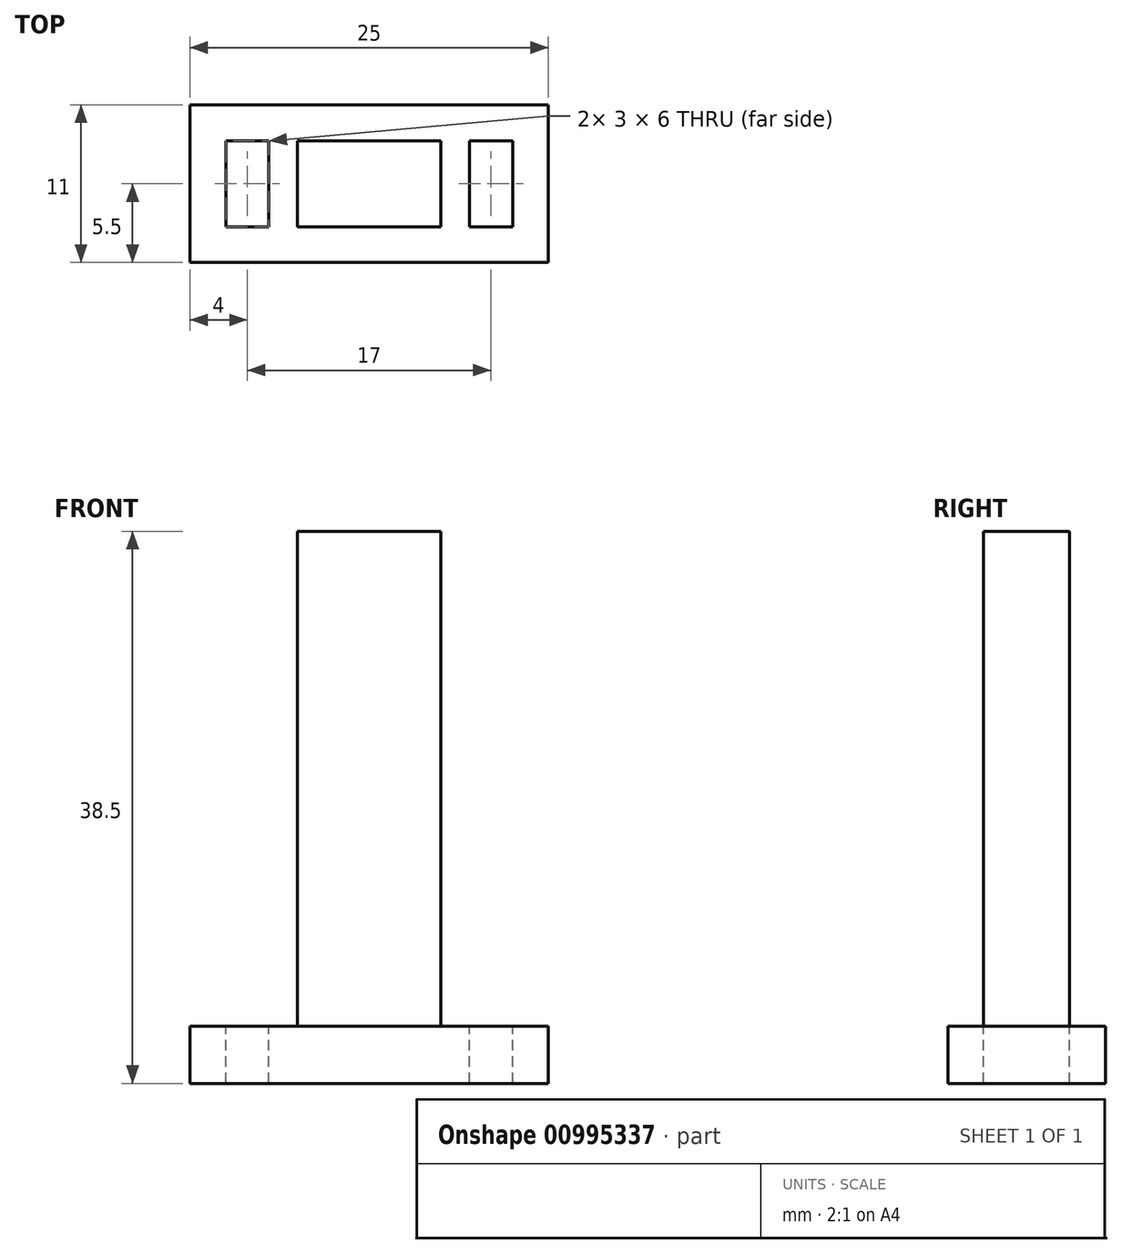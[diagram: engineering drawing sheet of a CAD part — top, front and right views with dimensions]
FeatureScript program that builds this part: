
annotation { "Feature Type Name" : "Feature", "Feature Type Description" : "" }
export const myFeature = defineFeature(function(context is Context, id is Id, definition is map)
    precondition{}
    {
        {
            var Q0;
            Q0=qCreatedBy(makeId("Top.planeOp"),FACE);
            var sketch = newSketch(context, id + "F0", { "sketchPlane" : qUnion([Q0])});
            skLineSegment(sketch, "E0.bottom", {"start": v(7.5, -5.5) * mm, "end": v(-7.5, -5.5) * mm});
            skLineSegment(sketch, "E0.top", {"start": v(7.5, 5.5) * mm, "end": v(-7.5, 5.5) * mm});
            skLineSegment(sketch, "E0.left", {"start": v(7.5, -5.5) * mm, "end": v(7.5, 5.5) * mm});
            skLineSegment(sketch, "E0.right", {"start": v(-7.5, -5.5) * mm, "end": v(-7.5, 5.5) * mm});
            skPoint(sketch, "E0.middle", {"position": v(0, 0) * mm});
            skPoint(sketch, "E1", {"position": v(5, 3) * mm});
            skPoint(sketch, "E2", {"position": v(5, -3) * mm});
            skPoint(sketch, "E3", {"position": v(10, 3) * mm});
            skPoint(sketch, "E4", {"position": v(10, -3) * mm});
            skPoint(sketch, "E5", {"position": v(10.73, -7.44) * mm});
            skLineSegment(sketch, "E6.bottom", {"start": v(7.5, 5.5) * mm, "end": v(12.5, 5.5) * mm});
            skLineSegment(sketch, "E6.top", {"start": v(7.5, -5.5) * mm, "end": v(12.5, -5.5) * mm});
            skLineSegment(sketch, "E6.left", {"start": v(7.5, 5.5) * mm, "end": v(7.5, -5.5) * mm});
            skLineSegment(sketch, "E6.right", {"start": v(12.5, 5.5) * mm, "end": v(12.5, -5.5) * mm});
            skLineSegment(sketch, "E7.bottom", {"start": v(-7.5, 5.5) * mm, "end": v(-12.5, 5.5) * mm});
            skLineSegment(sketch, "E7.top", {"start": v(-7.5, -5.5) * mm, "end": v(-12.5, -5.5) * mm});
            skLineSegment(sketch, "E7.left", {"start": v(-7.5, 5.5) * mm, "end": v(-7.5, -5.5) * mm});
            skLineSegment(sketch, "E7.right", {"start": v(-12.5, 5.5) * mm, "end": v(-12.5, -5.5) * mm});
            skSolve(sketch);
        }
        {
            var Q0;
            Q0=makeQuery(id+"F0.imprint","IMPRINT",FACE,{"disambiguationData":[TD([[makeQuery(id+"F0.imprint","IMPRINT",EDGE,{"derivedFrom":sQuery(id+"F0.wireOp",EDGE,"E0.bottom")}),-1.0]])]});
            extrude(context, id + "F1", {"entities" : qUnion([Q0]), "depth" : 4 * mm, "offsetDistance" : 25 * mm});
        }
        {
            var Q0;
            Q0=makeQuery(id+"F1.opExtrude","CAP_FACE",FACE,{"disambiguationData":[OSD([sQuery(id+"F0.wireOp",EDGE,"E0.bottom"),sQuery(id+"F0.wireOp",EDGE,"E0.top"),sQuery(id+"F0.wireOp",EDGE,"E0.left"),sQuery(id+"F0.wireOp",EDGE,"E0.right")])],"isStart":false});
            var sketch = newSketch(context, id + "F2", { "sketchPlane" : qUnion([Q0])});
            skLineSegment(sketch, "E8.bottom", {"start": v(-5, -3) * mm, "end": v(5, -3) * mm});
            skLineSegment(sketch, "E8.top", {"start": v(-5, 3) * mm, "end": v(5, 3) * mm});
            skLineSegment(sketch, "E8.left", {"start": v(-5, -3) * mm, "end": v(-5, 3) * mm});
            skLineSegment(sketch, "E8.right", {"start": v(5, -3) * mm, "end": v(5, 3) * mm});
            skPoint(sketch, "E8.middle", {"position": v(0, 0) * mm});
            skSolve(sketch);
        }
        {
            var Q0;
            Q0 = qSketchRegion(id + "F2", true);
            extrude(context, id + "F3", {"entities" : qUnion([Q0]), "operationType" : NewBodyOperationType.ADD, "depth" : 34.5 * mm, "offsetDistance" : 25 * mm});
        }
        {
            var Q0;
            Q0 = qSketchRegion(id + "F0", true);
            extrude(context, id + "F4", {"entities" : qUnion([Q0]), "operationType" : NewBodyOperationType.ADD, "depth" : 4 * mm, "offsetDistance" : 25 * mm});
        }
        {
            var Q0;
            {var subQ0=sQuery(id+"F0.wireOp",EDGE,"E0.top");var subQ1=sQuery(id+"F0.wireOp",EDGE,"E0.bottom");Q0=makeQuery(id+"F4.boolean.opBoolean","MERGE",FACE,{"derivedFrom":[makeQuery(id+"F1.opExtrude","CAP_FACE",FACE,{"disambiguationData":[OSD([subQ1,subQ0,sQuery(id+"F0.wireOp",EDGE,"E6.left"),sQuery(id+"F0.wireOp",EDGE,"E7.left")])],"isStart":false}),makeQuery(id+"F4.opExtrude","CAP_FACE",FACE,{"disambiguationData":[OSD([subQ1,subQ0,sQuery(id+"F0.wireOp",EDGE,"E6.bottom"),sQuery(id+"F0.wireOp",EDGE,"E6.top"),sQuery(id+"F0.wireOp",EDGE,"E6.right"),sQuery(id+"F0.wireOp",EDGE,"E7.bottom"),sQuery(id+"F0.wireOp",EDGE,"E7.top"),sQuery(id+"F0.wireOp",EDGE,"E7.right")])],"isStart":false})]});}
            var sketch = newSketch(context, id + "F5", { "sketchPlane" : qUnion([Q0])});
            skPoint(sketch, "E9", {"position": v(-12.25, 5.5) * mm});
            skLineSegment(sketch, "E10", {"start": v(-12.5, 5.5) * mm, "end": v(-7.04, 5.5) * mm});
            skLineSegment(sketch, "E11", {"start": v(-12.5, 5.5) * mm, "end": v(-12.5, -5.5) * mm});
            skLineSegment(sketch, "E12", {"start": v(-12.5, -5.5) * mm, "end": v(-12.5, -5.5) * mm});
            skPoint(sketch, "E13.bottom.start.orphan", {"position": v(-8.06, 0) * mm});
            skPoint(sketch, "E14.left.start.orphan", {"position": v(-12.25, 5.25) * mm});
            skPoint(sketch, "E15", {"position": v(-7, 3) * mm});
            skPoint(sketch, "E16", {"position": v(-10, 3) * mm});
            skPoint(sketch, "E17", {"position": v(-10, -3) * mm});
            skLineSegment(sketch, "E18.bottom", {"start": v(-10, -3) * mm, "end": v(-7, -3) * mm});
            skLineSegment(sketch, "E18.top", {"start": v(-10, 3) * mm, "end": v(-7, 3) * mm});
            skLineSegment(sketch, "E18.left", {"start": v(-10, -3) * mm, "end": v(-10, 3) * mm});
            skLineSegment(sketch, "E18.right", {"start": v(-7, -3) * mm, "end": v(-7, 3) * mm});
            skPoint(sketch, "E19", {"position": v(5, 3) * mm});
            skPoint(sketch, "E20", {"position": v(7, 3) * mm});
            skPoint(sketch, "E21", {"position": v(10, 3) * mm});
            skPoint(sketch, "E22", {"position": v(10, -3) * mm});
            skLineSegment(sketch, "E23.bottom", {"start": v(10, -3) * mm, "end": v(7, -3) * mm});
            skLineSegment(sketch, "E23.top", {"start": v(10, 3) * mm, "end": v(7, 3) * mm});
            skLineSegment(sketch, "E23.left", {"start": v(10, -3) * mm, "end": v(10, 3) * mm});
            skLineSegment(sketch, "E23.right", {"start": v(7, -3) * mm, "end": v(7, 3) * mm});
            skSolve(sketch);
        }
        {
            var Q0;
            Q0 = qSketchRegion(id + "F5", true);
            extrude(context, id + "F6", {"entities" : qUnion([Q0]), "operationType" : NewBodyOperationType.REMOVE, "oppositeDirection" : true, "depth" : 4 * mm, "offsetDistance" : 25 * mm});
        }
    });
